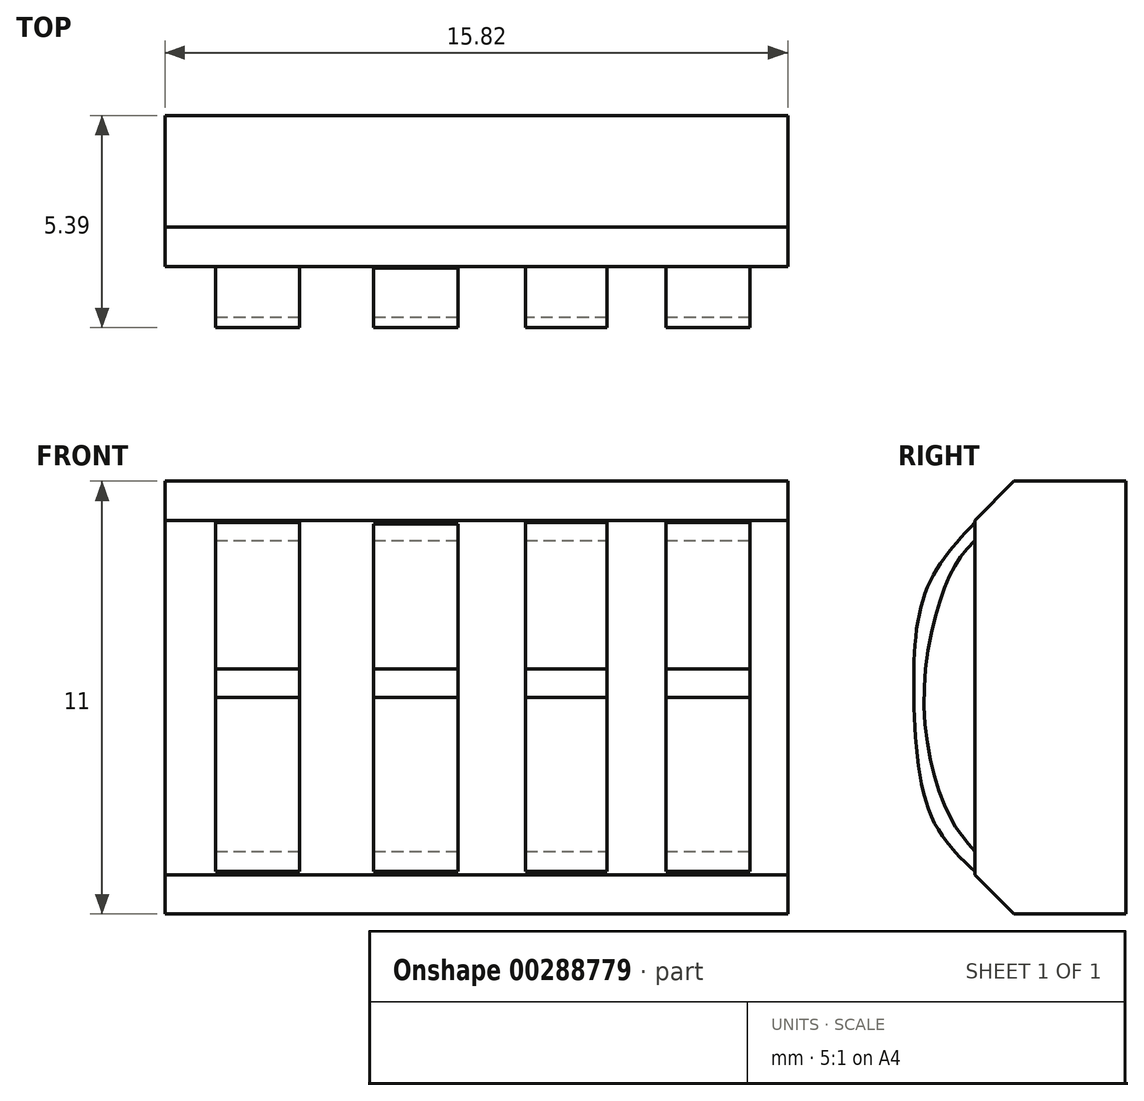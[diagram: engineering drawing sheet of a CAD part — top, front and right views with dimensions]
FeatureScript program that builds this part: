
annotation { "Feature Type Name" : "Feature", "Feature Type Description" : "" }
export const myFeature = defineFeature(function(context is Context, id is Id, definition is map)
    precondition{}
    {
        {
            var Q0;
            Q0=qCreatedBy(makeId("Front.planeOp"),FACE);
            cPlane(context, id + "F0", {"entities" : qUnion([Q0]), "cplaneType" : CPlaneType.OFFSET, "offset" : 25 * mm, "width" : 150 * mm, "height" : 150 * mm});
        }
        {
            var Q0;
            Q0=qCreatedBy(id+"F0.planeOp",FACE);
            var sketch = newSketch(context, id + "F1", { "sketchPlane" : qUnion([Q0])});
            skLineSegment(sketch, "E0.bottom", {"start": v(7.9, 5.5) * mm, "end": v(-7.9, 5.5) * mm});
            skLineSegment(sketch, "E0.top", {"start": v(7.9, -5.5) * mm, "end": v(-7.91, -5.5) * mm});
            skLineSegment(sketch, "E0.left", {"start": v(7.9, 5.5) * mm, "end": v(7.9, -5.5) * mm});
            skLineSegment(sketch, "E0.right", {"start": v(-7.91, 5.5) * mm, "end": v(-7.91, -5.5) * mm});
            skPoint(sketch, "E0.middle", {"position": v(0, 0) * mm});
            skSolve(sketch);
        }
        {
            var Q0;
            Q0=makeQuery(id+"F1.imprint","IMPRINT",FACE,{"disambiguationData":[TD([[makeQuery(id+"F1.imprint","IMPRINT",EDGE,{"derivedFrom":sQuery(id+"F1.wireOp",EDGE,"E0.bottom")}),1.0]])]});
            extrude(context, id + "F2", {"entities" : qUnion([Q0]), "depth" : 3.84 * mm});
        }
        {
            var Q0;
            Q0=makeQuery(id+"F2.opExtrude","CAP_EDGE",EDGE,{"disambiguationData":[OSD([sQuery(id+"F1.wireOp",EDGE,"E0.bottom")])],"isStart":false});
            chamfer(context, id + "F3", {"entities" : qUnion([Q0]), "width" : 1 * mm, "tangentPropagation" : true});
        }
        {
            var Q0;
            Q0=makeQuery(id+"F2.opExtrude","CAP_EDGE",EDGE,{"disambiguationData":[OSD([sQuery(id+"F1.wireOp",EDGE,"E0.top")])],"isStart":false});
            chamfer(context, id + "F4", {"entities" : qUnion([Q0]), "width" : 1 * mm, "tangentPropagation" : true});
        }
        {
            var Q0;
            Q0=makeQuery(id+"F2.opExtrude","CAP_FACE",FACE,{"disambiguationData":[OSD([sQuery(id+"F1.wireOp",EDGE,"E0.bottom"),sQuery(id+"F1.wireOp",EDGE,"E0.top"),sQuery(id+"F1.wireOp",EDGE,"E0.left"),sQuery(id+"F1.wireOp",EDGE,"E0.right")])],"isStart":false});
            var sketch = newSketch(context, id + "F5", { "sketchPlane" : qUnion([Q0])});
            skLineSegment(sketch, "E1.bottom", {"start": v(-6.63, -4.5) * mm, "end": v(-4.49, -4.5) * mm});
            skLineSegment(sketch, "E1.top", {"start": v(-6.63, 4.5) * mm, "end": v(-4.49, 4.5) * mm});
            skLineSegment(sketch, "E1.left", {"start": v(-6.63, -4.5) * mm, "end": v(-6.63, 4.5) * mm});
            skLineSegment(sketch, "E1.right", {"start": v(-4.49, -4.5) * mm, "end": v(-4.49, 4.5) * mm});
            skLineSegment(sketch, "E2.bottom", {"start": v(-2.61, -4.48) * mm, "end": v(-0.47, -4.48) * mm});
            skLineSegment(sketch, "E2.top", {"start": v(-2.61, 4.4) * mm, "end": v(-0.47, 4.4) * mm});
            skLineSegment(sketch, "E2.left", {"start": v(-2.61, -4.48) * mm, "end": v(-2.61, 4.4) * mm});
            skLineSegment(sketch, "E2.right", {"start": v(-0.47, -4.48) * mm, "end": v(-0.47, 4.4) * mm});
            skLineSegment(sketch, "E3.bottom", {"start": v(1.25, -4.44) * mm, "end": v(3.31, -4.44) * mm});
            skLineSegment(sketch, "E3.top", {"start": v(1.25, 4.45) * mm, "end": v(3.31, 4.45) * mm});
            skLineSegment(sketch, "E3.left", {"start": v(3.31, -4.44) * mm, "end": v(3.31, 4.45) * mm});
            skLineSegment(sketch, "E3.right", {"start": v(1.25, -4.44) * mm, "end": v(1.25, 4.45) * mm});
            skLineSegment(sketch, "E4.bottom", {"start": v(4.81, -4.42) * mm, "end": v(6.95, -4.42) * mm});
            skLineSegment(sketch, "E4.top", {"start": v(4.81, 4.45) * mm, "end": v(6.95, 4.45) * mm});
            skLineSegment(sketch, "E4.left", {"start": v(4.81, -4.42) * mm, "end": v(4.81, 4.45) * mm});
            skLineSegment(sketch, "E4.right", {"start": v(6.95, -4.42) * mm, "end": v(6.95, 4.45) * mm});
            skSolve(sketch);
        }
        {
            var Q0;
            Q0=makeQuery(id+"F5.imprint","IMPRINT",FACE,{"disambiguationData":[TD([[makeQuery(id+"F5.imprint","IMPRINT",EDGE,{"derivedFrom":sQuery(id+"F5.wireOp",EDGE,"E4.bottom")}),1.0]])]});
            var Q1;
            Q1=makeQuery(id+"F5.imprint","IMPRINT",FACE,{"disambiguationData":[TD([[makeQuery(id+"F5.imprint","IMPRINT",EDGE,{"derivedFrom":sQuery(id+"F5.wireOp",EDGE,"E3.bottom")}),1.0]])]});
            var Q2;
            Q2=makeQuery(id+"F5.imprint","IMPRINT",FACE,{"disambiguationData":[TD([[makeQuery(id+"F5.imprint","IMPRINT",EDGE,{"derivedFrom":sQuery(id+"F5.wireOp",EDGE,"E2.bottom")}),1.0]])]});
            var Q3;
            Q3=makeQuery(id+"F5.imprint","IMPRINT",FACE,{"disambiguationData":[TD([[makeQuery(id+"F5.imprint","IMPRINT",EDGE,{"derivedFrom":sQuery(id+"F5.wireOp",EDGE,"E1.bottom")}),1.0]])]});
            extrude(context, id + "F6", {"entities" : qUnion([Q0, Q1, Q2, Q3]), "depth" : 1.55 * mm});
        }
        {
            var Q0;
            Q0=makeQuery(id+"F6.opExtrude","SWEPT_FACE",FACE,{"disambiguationData":[OSD([sQuery(id+"F5.wireOp",EDGE,"E4.right")])]});
            var sketch = newSketch(context, id + "F7", { "sketchPlane" : qUnion([Q0])});
            skLineSegment(sketch, "E5", {"start": v(-30.4, -4.42) * mm, "end": v(-30.4, 4.45) * mm});
            skLineSegment(sketch, "E6", {"start": v(-30.4, 4.45) * mm, "end": v(-30.4, -4.42) * mm});
            skFitSpline(sketch, "E7", {"points": [v(-28.84, -4.42) * mm, v(-29.94, -3.02) * mm, v(-30.4, 0) * mm, v(-30.05, 2.78) * mm, v(-28.84, 4.45) * mm], "startDerivative": vector(-5.81, 5.51) * mm, "endDerivative": vector(6.09, 6.52) * mm});
            skLineSegment(sketch, "E8", {"start": v(-28.84, -4.42) * mm, "end": v(-28.84, -3.9) * mm});
            skLineSegment(sketch, "E9", {"start": v(-28.84, -3.9) * mm, "end": v(-28.84, 3.99) * mm});
            skLineSegment(sketch, "E10", {"start": v(-28.84, 3.99) * mm, "end": v(-28.84, 4.45) * mm});
            skFitSpline(sketch, "E11", {"points": [v(-28.84, -3.9) * mm, v(-29.55, -2.86) * mm, v(-30.13, 0) * mm, v(-29.55, 2.93) * mm, v(-28.84, 3.99) * mm], "startDerivative": vector(-3.86, 4.47) * mm, "endDerivative": vector(4.8, 4.87) * mm});
            skLineSegment(sketch, "E12", {"start": v(-28.84, -4.42) * mm, "end": v(-30.4, -4.42) * mm});
            skLineSegment(sketch, "E13", {"start": v(-30.4, 0) * mm, "end": v(-30.4, -4.42) * mm});
            skLineSegment(sketch, "E14", {"start": v(-30.4, 0) * mm, "end": v(-30.4, 4.45) * mm});
            skLineSegment(sketch, "E15", {"start": v(-28.84, 4.45) * mm, "end": v(-30.4, 4.45) * mm});
            skLineSegment(sketch, "E16", {"start": v(-30.4, 4.45) * mm, "end": v(-30.4, 4.78) * mm});
            skLineSegment(sketch, "E17", {"start": v(-30.4, 4.78) * mm, "end": v(-28.84, 4.45) * mm});
            skLineSegment(sketch, "E18", {"start": v(-30.4, 4.78) * mm, "end": v(-28.84, 4.7) * mm});
            skLineSegment(sketch, "E19", {"start": v(-28.84, 4.7) * mm, "end": v(-28.84, 4.45) * mm});
            skLineSegment(sketch, "E20", {"start": v(-30.4, -4.42) * mm, "end": v(-30.4, -4.57) * mm});
            skLineSegment(sketch, "E21", {"start": v(-30.4, -4.57) * mm, "end": v(-28.84, -4.7) * mm});
            skLineSegment(sketch, "E22", {"start": v(-28.84, -4.7) * mm, "end": v(-28.84, -4.42) * mm});
            skSolve(sketch);
        }
        {
            var Q0;
            {var subQ0=sQuery(id+"F7.wireOp",EDGE,"E14");var subQ1=sQuery(id+"F7.wireOp",EDGE,"E7");var subQ3=makeQuery(id+"F7.imprint","INTERSECT",VERTEX,{"derivedFrom":[subQ1,subQ0]});Q0=makeQuery(id+"F7.imprint","IMPRINT",FACE,{"disambiguationData":[TD([[makeQuery(id+"F7.imprint","IMPRINT",EDGE,{"disambiguationData":[TD([[subQ3,1.0]])],"derivedFrom":subQ1}),-1.0]])]});}
            var Q1;
            {var subQ0=sQuery(id+"F7.wireOp",EDGE,"E15");Q1=makeQuery(id+"F7.imprint","IMPRINT",FACE,{"disambiguationData":[TD([[makeQuery(id+"F7.imprint","IMPRINT",EDGE,{"derivedFrom":subQ0}),-1.0]])]});}
            var Q2;
            Q2=makeQuery(id+"F7.imprint","IMPRINT",FACE,{"disambiguationData":[TD([[makeQuery(id+"F7.imprint","IMPRINT",EDGE,{"derivedFrom":sQuery(id+"F7.wireOp",EDGE,"E11")}),-1.0]])]});
            var Q3;
            {var subQ0=sQuery(id+"F7.wireOp",EDGE,"E12");Q3=makeQuery(id+"F7.imprint","IMPRINT",FACE,{"disambiguationData":[TD([[makeQuery(id+"F7.imprint","IMPRINT",EDGE,{"derivedFrom":subQ0}),1.0]])]});}
            var Q4;
            Q4=makeQuery(id+"F7.imprint","IMPRINT",FACE,{"disambiguationData":[TD([[makeQuery(id+"F7.imprint","IMPRINT",EDGE,{"derivedFrom":sQuery(id+"F7.wireOp",EDGE,"E15")}),1.0]])]});
            var Q5;
            Q5=makeQuery(id+"F7.imprint","IMPRINT",FACE,{"disambiguationData":[TD([[makeQuery(id+"F7.imprint","IMPRINT",EDGE,{"derivedFrom":sQuery(id+"F7.wireOp",EDGE,"E17")}),1.0]])]});
            var Q6;
            Q6=makeQuery(id+"F7.imprint","IMPRINT",FACE,{"disambiguationData":[TD([[makeQuery(id+"F7.imprint","IMPRINT",EDGE,{"derivedFrom":sQuery(id+"F7.wireOp",EDGE,"E12")}),-1.0]])]});
            extrude(context, id + "F8", {"entities" : qUnion([Q0, Q1, Q2, Q3, Q4, Q5, Q6]), "operationType" : NewBodyOperationType.REMOVE, "oppositeDirection" : true, "depth" : 25 * mm});
        }
    });
